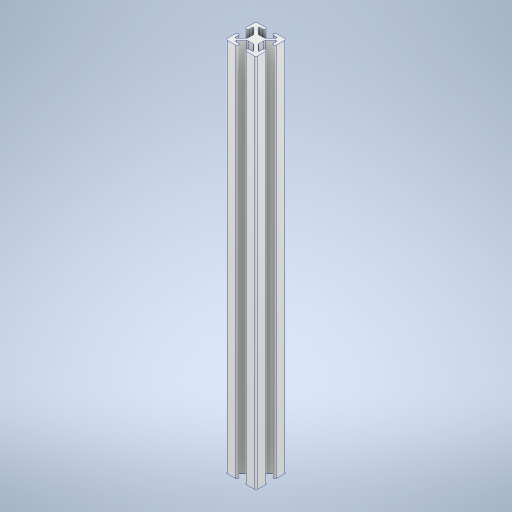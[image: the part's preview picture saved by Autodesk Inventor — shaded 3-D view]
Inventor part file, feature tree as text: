
AUTODESK INVENTOR PART (.ipt)
format: ipt  version: 2024 (Build 280153000, 153)  size: 345,088 bytes
history: native  units: in
note: dims shown in document units (in); Inventor stores cm internally (conversion verified against a paired STEP export)
features: fillet x2, extrude x1, sketch x1
ambient origin geometry x8: Origin, YZ Plane, XZ Plane, XY Plane, X Axis, Y Axis, Z Axis, Center Point
bodies: Solid1 (feature_tree)
feature tree (4):
  extrude  "Extrusion1"  Depth=1.0in
  fillet  "Fillet1"  Radius=0.8in
  fillet  "Fillet2"  Radius=0.8in
  sketch  "Sketch1"  dims[d0=1.0in d1=1.0in d2=0.8in d3=0.8in d4=0.35in d5=0.35in d6=0.125in d7=0.25in d8=0.125in d9=0.25in d10=0.1in d11=0.1in d12=12.35in d13=0.0in d14=0.05in d15=0.025in]
